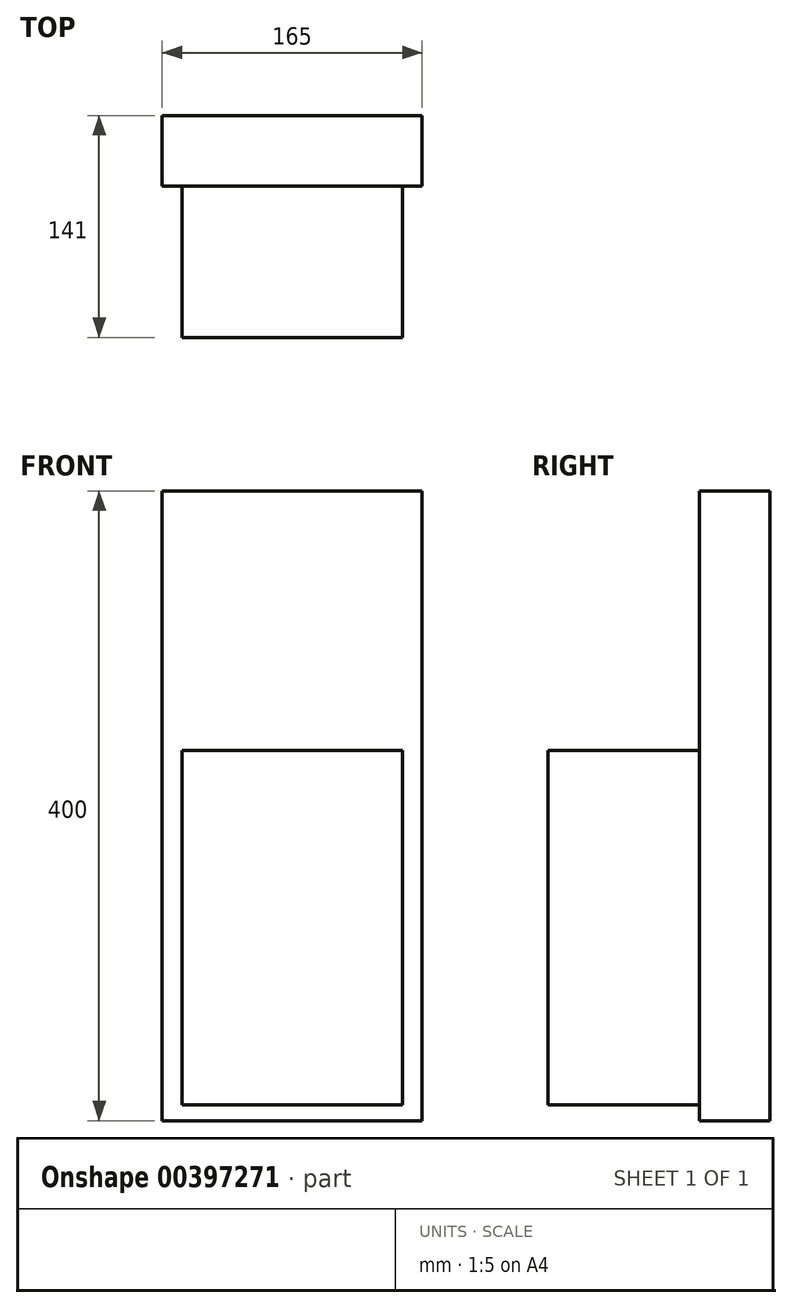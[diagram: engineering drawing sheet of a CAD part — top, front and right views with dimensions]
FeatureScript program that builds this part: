
annotation { "Feature Type Name" : "Feature", "Feature Type Description" : "" }
export const myFeature = defineFeature(function(context is Context, id is Id, definition is map)
    precondition{}
    {
        {
            var Q0;
            Q0=qCreatedBy(makeId("Right.planeOp"),FACE);
            var sketch = newSketch(context, id + "F0", { "sketchPlane" : qUnion([Q0])});
            skLineSegment(sketch, "E0.bottom", {"start": v(-22.5, -200) * mm, "end": v(22.5, -200) * mm});
            skLineSegment(sketch, "E0.top", {"start": v(-22.5, 200) * mm, "end": v(22.5, 200) * mm});
            skLineSegment(sketch, "E0.left", {"start": v(-22.5, -200) * mm, "end": v(-22.5, 200) * mm});
            skLineSegment(sketch, "E0.right", {"start": v(22.5, -200) * mm, "end": v(22.5, 200) * mm});
            skPoint(sketch, "E0.middle", {"position": v(0, 0) * mm});
            skPoint(sketch, "E1.middle", {"position": v(-21.6, 0) * mm});
            skLineSegment(sketch, "E2", {"start": v(-118.5, 35) * mm, "end": v(-22.5, 35) * mm});
            skLineSegment(sketch, "E3", {"start": v(-118.5, -190) * mm, "end": v(-22.5, -190) * mm});
            skLineSegment(sketch, "E4", {"start": v(-118.5, 35) * mm, "end": v(-118.5, -190) * mm});
            skSolve(sketch);
        }
        {
            var Q0;
            {var subQ0=sQuery(id+"F0.wireOp",EDGE,"E2");Q0=makeQuery(id+"F0.imprint","IMPRINT",FACE,{"disambiguationData":[TD([[makeQuery(id+"F0.imprint","IMPRINT",EDGE,{"derivedFrom":subQ0}),-1.0]])]});}
            extrude(context, id + "F1", {"entities" : qUnion([Q0]), "endBound" : BoundingType.SYMMETRIC, "depth" : 140 * mm});
        }
        {
            var Q0;
            {var subQ3=sQuery(id+"F0.wireOp",EDGE,"E0.bottom");Q0=makeQuery(id+"F0.imprint","IMPRINT",FACE,{"disambiguationData":[TD([[makeQuery(id+"F0.imprint","IMPRINT",EDGE,{"derivedFrom":subQ3}),1.0]])]});}
            var Q1;
            Q1 = qSketchRegion(id + "FhEGldEUfTZpI5D_2", true);
            extrude(context, id + "F2", {"entities" : qUnion([Q0, Q1]), "endBound" : BoundingType.SYMMETRIC, "depth" : 165 * mm});
        }
    });
